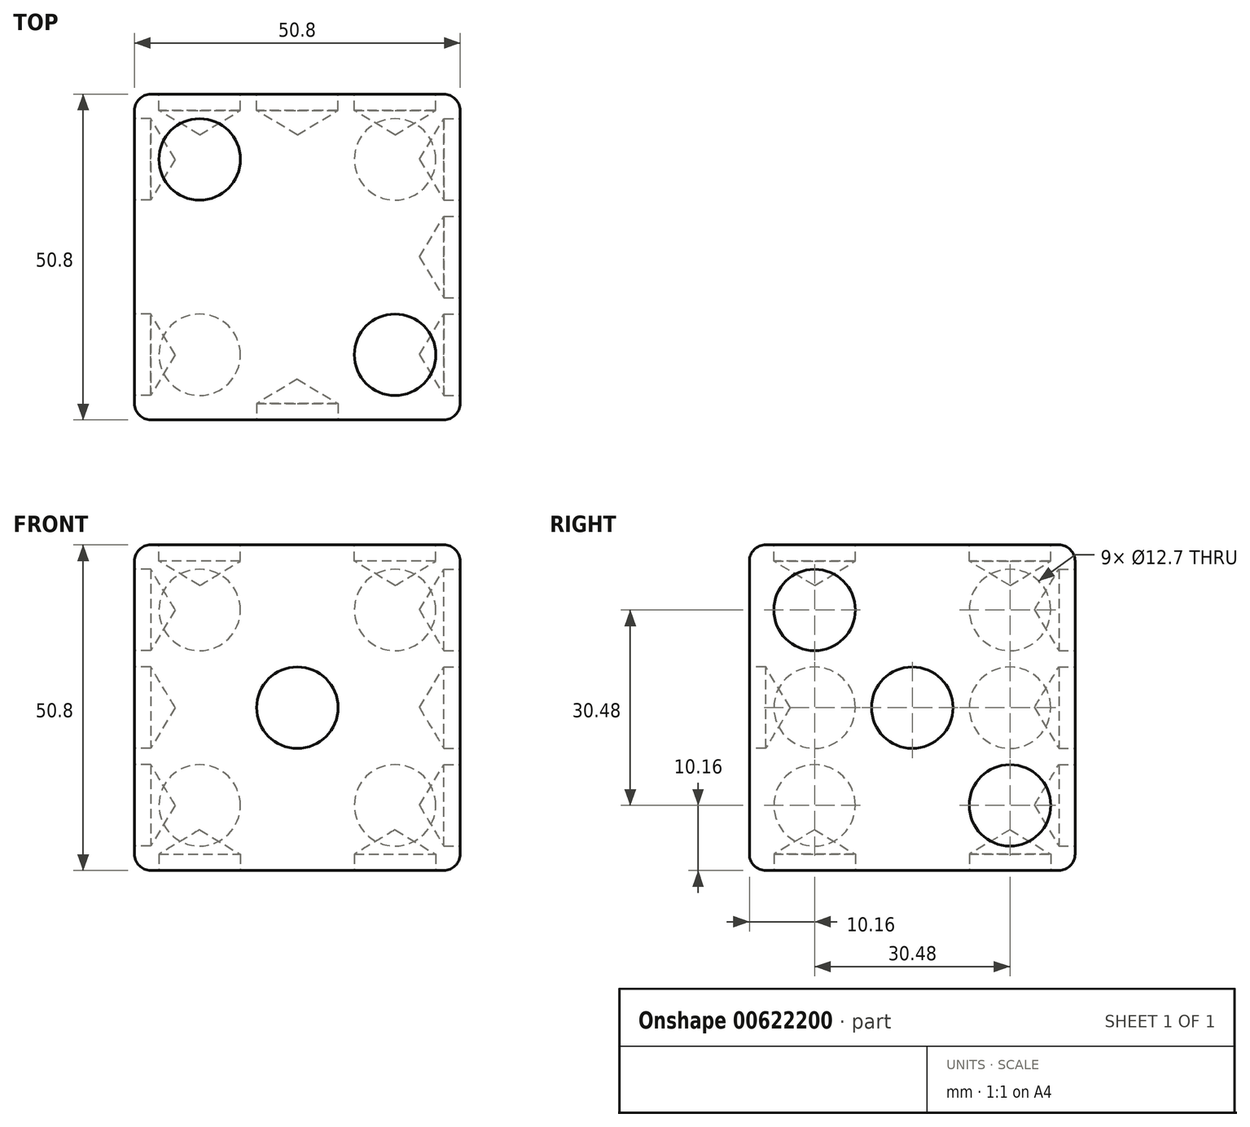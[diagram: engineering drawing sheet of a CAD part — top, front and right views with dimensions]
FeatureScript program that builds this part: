
annotation { "Feature Type Name" : "Feature", "Feature Type Description" : "" }
export const myFeature = defineFeature(function(context is Context, id is Id, definition is map)
    precondition{}
    {
        {
            var Q0;
            Q0=qCreatedBy(makeId("Front.planeOp"),FACE);
            var sketch = newSketch(context, id + "F0", { "sketchPlane" : qUnion([Q0])});
            skLineSegment(sketch, "E0.bottom", {"start": v(25.4, -25.4) * mm, "end": v(-25.4, -25.4) * mm});
            skLineSegment(sketch, "E0.top", {"start": v(25.4, 25.4) * mm, "end": v(-25.4, 25.4) * mm});
            skLineSegment(sketch, "E0.left", {"start": v(25.4, -25.4) * mm, "end": v(25.4, 25.4) * mm});
            skLineSegment(sketch, "E0.right", {"start": v(-25.4, -25.4) * mm, "end": v(-25.4, 25.4) * mm});
            skPoint(sketch, "E0.middle", {"position": v(0, 0) * mm});
            skSolve(sketch);
        }
        {
            var Q0;
            Q0 = qSketchRegion(id + "F0", true);
            extrude(context, id + "F1", {"entities" : qUnion([Q0]), "endBound" : BoundingType.SYMMETRIC, "depth" : 50.8 * mm, "offsetDistance" : 25.4 * mm});
        }
        {
            var Q0;
            Q0=makeQuery(id+"F1.opExtrude","CAP_FACE",FACE,{"disambiguationData":[OSD([sQuery(id+"F0.wireOp",EDGE,"E0.bottom"),sQuery(id+"F0.wireOp",EDGE,"E0.top"),sQuery(id+"F0.wireOp",EDGE,"E0.left"),sQuery(id+"F0.wireOp",EDGE,"E0.right")])],"isStart":false});
            var sketch = newSketch(context, id + "F2", { "sketchPlane" : qUnion([Q0])});
            skCircle(sketch, "E1", {"center": v(0, 0) * mm, "radius": 6.35 * mm});
            skSolve(sketch);
        }
        {
            var Q0;
            Q0=sQuery(id+"F2.wireOp",VERTEX,"E1.center");
            var Q1;
            Q1=makeQuery(id+"F1.opExtrude","SWEPT_BODY",BODY,{"disambiguationData":[OSD([sQuery(id+"F0.wireOp",EDGE,"E0.bottom"),sQuery(id+"F0.wireOp",EDGE,"E0.top"),sQuery(id+"F0.wireOp",EDGE,"E0.left"),sQuery(id+"F0.wireOp",EDGE,"E0.right")])]});
            hole(context, id + "F3", {"style" : HoleStyle.SIMPLE, "endStyle" : HoleEndStyle.BLIND, "holeDiameter" : 12.7 * mm, "majorDiameter" : 6.35 * mm, "holeDepth" : 2.54 * mm, "isTappedThrough" : true, "tappedDepth" : 12.7 * mm, "tapClearance" : 3, "startFromSketch" : true, "locations" : qUnion([Q0]), "scope" : qUnion([Q1])});
        }
        {
            var Q0;
            Q0=makeQuery(id+"F1.opExtrude","CAP_FACE",FACE,{"disambiguationData":[OSD([sQuery(id+"F0.wireOp",EDGE,"E0.bottom"),sQuery(id+"F0.wireOp",EDGE,"E0.top"),sQuery(id+"F0.wireOp",EDGE,"E0.left"),sQuery(id+"F0.wireOp",EDGE,"E0.right")])],"isStart":true});
            var sketch = newSketch(context, id + "F4", { "sketchPlane" : qUnion([Q0])});
            skCircle(sketch, "E2", {"center": v(0, 0) * mm, "radius": 6.35 * mm});
            skCircle(sketch, "E3", {"center": v(-15.24, 15.24) * mm, "radius": 6.35 * mm});
            skCircle(sketch, "E4", {"center": v(15.24, -15.24) * mm, "radius": 6.35 * mm});
            skSolve(sketch);
        }
        {
            var Q0;
            Q0=sQuery(id+"F4.wireOp",VERTEX,"E3.center");
            var Q1;
            Q1=sQuery(id+"F4.wireOp",VERTEX,"E2.center");
            var Q2;
            Q2=sQuery(id+"F4.wireOp",VERTEX,"E4.center");
            var Q3;
            Q3=makeQuery(id+"F1.opExtrude","SWEPT_BODY",BODY,{"disambiguationData":[OSD([sQuery(id+"F0.wireOp",EDGE,"E0.bottom"),sQuery(id+"F0.wireOp",EDGE,"E0.top"),sQuery(id+"F0.wireOp",EDGE,"E0.left"),sQuery(id+"F0.wireOp",EDGE,"E0.right")])]});
            hole(context, id + "F5", {"style" : HoleStyle.SIMPLE, "endStyle" : HoleEndStyle.BLIND, "holeDiameter" : 12.7 * mm, "majorDiameter" : 6.35 * mm, "holeDepth" : 2.54 * mm, "isTappedThrough" : true, "tappedDepth" : 12.7 * mm, "tapClearance" : 3, "startFromSketch" : true, "locations" : qUnion([Q0, Q1, Q2]), "scope" : qUnion([Q3])});
        }
        {
            var Q0;
            Q0=makeQuery(id+"F1.opExtrude","SWEPT_FACE",FACE,{"disambiguationData":[OSD([sQuery(id+"F0.wireOp",EDGE,"E0.top")])]});
            var sketch = newSketch(context, id + "F6", { "sketchPlane" : qUnion([Q0])});
            skCircle(sketch, "E5", {"center": v(-15.24, 15.24) * mm, "radius": 6.35 * mm});
            skCircle(sketch, "E6", {"center": v(15.24, -15.24) * mm, "radius": 6.35 * mm});
            skSolve(sketch);
        }
        {
            var Q0;
            Q0=sQuery(id+"F6.wireOp",VERTEX,"E5.center");
            var Q1;
            Q1=sQuery(id+"F6.wireOp",VERTEX,"E6.center");
            var Q2;
            Q2=makeQuery(id+"F1.opExtrude","SWEPT_BODY",BODY,{"disambiguationData":[OSD([sQuery(id+"F0.wireOp",EDGE,"E0.bottom"),sQuery(id+"F0.wireOp",EDGE,"E0.top"),sQuery(id+"F0.wireOp",EDGE,"E0.left"),sQuery(id+"F0.wireOp",EDGE,"E0.right")])]});
            hole(context, id + "F7", {"style" : HoleStyle.SIMPLE, "endStyle" : HoleEndStyle.BLIND, "holeDiameter" : 12.7 * mm, "majorDiameter" : 6.35 * mm, "holeDepth" : 2.54 * mm, "isTappedThrough" : true, "tappedDepth" : 12.7 * mm, "tapClearance" : 3, "startFromSketch" : true, "locations" : qUnion([Q0, Q1]), "scope" : qUnion([Q2])});
        }
        {
            var Q0;
            Q0=makeQuery(id+"F1.opExtrude","SWEPT_FACE",FACE,{"disambiguationData":[OSD([sQuery(id+"F0.wireOp",EDGE,"E0.bottom")])]});
            var sketch = newSketch(context, id + "F8", { "sketchPlane" : qUnion([Q0])});
            skCircle(sketch, "E7", {"center": v(-15.24, 15.24) * mm, "radius": 6.35 * mm});
            skCircle(sketch, "E8", {"center": v(15.24, 15.24) * mm, "radius": 6.35 * mm});
            skCircle(sketch, "E9", {"center": v(-15.24, -15.24) * mm, "radius": 6.35 * mm});
            skCircle(sketch, "E10", {"center": v(15.24, -15.24) * mm, "radius": 6.35 * mm});
            skSolve(sketch);
        }
        {
            var Q0;
            Q0=sQuery(id+"F8.wireOp",VERTEX,"E7.center");
            var Q1;
            Q1=sQuery(id+"F8.wireOp",VERTEX,"E8.center");
            var Q2;
            Q2=sQuery(id+"F8.wireOp",VERTEX,"E10.center");
            var Q3;
            Q3=sQuery(id+"F8.wireOp",VERTEX,"E9.center");
            var Q4;
            Q4=makeQuery(id+"F1.opExtrude","SWEPT_BODY",BODY,{"disambiguationData":[OSD([sQuery(id+"F0.wireOp",EDGE,"E0.bottom"),sQuery(id+"F0.wireOp",EDGE,"E0.top"),sQuery(id+"F0.wireOp",EDGE,"E0.left"),sQuery(id+"F0.wireOp",EDGE,"E0.right")])]});
            hole(context, id + "F9", {"style" : HoleStyle.SIMPLE, "endStyle" : HoleEndStyle.BLIND, "holeDiameter" : 12.7 * mm, "majorDiameter" : 6.35 * mm, "holeDepth" : 2.54 * mm, "isTappedThrough" : true, "tappedDepth" : 12.7 * mm, "tapClearance" : 3, "startFromSketch" : true, "locations" : qUnion([Q0, Q1, Q2, Q3]), "scope" : qUnion([Q4])});
        }
        {
            var Q0;
            Q0=makeQuery(id+"F1.opExtrude","CAP_FACE",FACE,{"disambiguationData":[OSD([sQuery(id+"F0.wireOp",EDGE,"E0.bottom"),sQuery(id+"F0.wireOp",EDGE,"E0.top"),sQuery(id+"F0.wireOp",EDGE,"E0.left"),sQuery(id+"F0.wireOp",EDGE,"E0.right")])],"isStart":true});
            var sketch = newSketch(context, id + "F10", { "sketchPlane" : qUnion([Q0])});
            skSolve(sketch);
        }
        {
            var Q0;
            Q0=makeQuery(id+"F10.imprint","IMPRINT",FACE,{"disambiguationData":[TD([[makeQuery(id+"F10.imprint","IMPRINT",EDGE,{"derivedFrom":makeQuery(id+"F1.opExtrude","CAP_EDGE",EDGE,{"disambiguationData":[OSD([sQuery(id+"F0.wireOp",EDGE,"E0.bottom")])],"isStart":true})}),1.0]])]});
            var sketch = newSketch(context, id + "F11", { "sketchPlane" : qUnion([Q0])});
            skCircle(sketch, "E11", {"center": v(15.24, 15.24) * mm, "radius": 6.35 * mm});
            skCircle(sketch, "E12", {"center": v(-15.24, -15.24) * mm, "radius": 6.35 * mm});
            skSolve(sketch);
        }
        {
            var Q0;
            Q0=sQuery(id+"F11.wireOp",VERTEX,"E11.center");
            var Q1;
            Q1=sQuery(id+"F11.wireOp",VERTEX,"E12.center");
            var Q2;
            Q2=makeQuery(id+"F1.opExtrude","SWEPT_BODY",BODY,{"disambiguationData":[OSD([sQuery(id+"F0.wireOp",EDGE,"E0.bottom"),sQuery(id+"F0.wireOp",EDGE,"E0.top"),sQuery(id+"F0.wireOp",EDGE,"E0.left"),sQuery(id+"F0.wireOp",EDGE,"E0.right")])]});
            hole(context, id + "F12", {"style" : HoleStyle.SIMPLE, "endStyle" : HoleEndStyle.BLIND, "holeDiameter" : 12.7 * mm, "majorDiameter" : 6.35 * mm, "holeDepth" : 2.54 * mm, "isTappedThrough" : true, "tappedDepth" : 12.7 * mm, "tapClearance" : 3, "startFromSketch" : true, "locations" : qUnion([Q0, Q1]), "scope" : qUnion([Q2])});
        }
        {
            var Q0;
            Q0=makeQuery(id+"F1.opExtrude","SWEPT_FACE",FACE,{"disambiguationData":[OSD([sQuery(id+"F0.wireOp",EDGE,"E0.left")])]});
            var sketch = newSketch(context, id + "F13", { "sketchPlane" : qUnion([Q0])});
            skCircle(sketch, "E13", {"center": v(-15.24, 15.24) * mm, "radius": 6.35 * mm});
            skCircle(sketch, "E14", {"center": v(0, 0) * mm, "radius": 6.35 * mm});
            skCircle(sketch, "E15", {"center": v(15.24, -15.24) * mm, "radius": 6.35 * mm});
            skSolve(sketch);
        }
        {
            var Q0;
            Q0=sQuery(id+"F13.wireOp",VERTEX,"E13.center");
            var Q1;
            Q1=sQuery(id+"F13.wireOp",VERTEX,"E14.center");
            var Q2;
            Q2=sQuery(id+"F13.wireOp",VERTEX,"E15.center");
            var Q3;
            Q3=makeQuery(id+"F1.opExtrude","SWEPT_BODY",BODY,{"disambiguationData":[OSD([sQuery(id+"F0.wireOp",EDGE,"E0.bottom"),sQuery(id+"F0.wireOp",EDGE,"E0.top"),sQuery(id+"F0.wireOp",EDGE,"E0.left"),sQuery(id+"F0.wireOp",EDGE,"E0.right")])]});
            hole(context, id + "F14", {"style" : HoleStyle.SIMPLE, "endStyle" : HoleEndStyle.BLIND, "holeDiameter" : 12.7 * mm, "majorDiameter" : 6.35 * mm, "holeDepth" : 2.54 * mm, "isTappedThrough" : true, "tappedDepth" : 12.7 * mm, "tapClearance" : 3, "startFromSketch" : true, "locations" : qUnion([Q0, Q1, Q2]), "scope" : qUnion([Q3])});
        }
        {
            var Q0;
            Q0=makeQuery(id+"F1.opExtrude","SWEPT_FACE",FACE,{"disambiguationData":[OSD([sQuery(id+"F0.wireOp",EDGE,"E0.right")])]});
            var sketch = newSketch(context, id + "F15", { "sketchPlane" : qUnion([Q0])});
            skCircle(sketch, "E16", {"center": v(-15.24, 15.24) * mm, "radius": 6.35 * mm});
            skCircle(sketch, "E17", {"center": v(-15.24, 0) * mm, "radius": 6.35 * mm});
            skCircle(sketch, "E18", {"center": v(-15.24, -15.24) * mm, "radius": 6.35 * mm});
            skCircle(sketch, "E19", {"center": v(15.24, 15.24) * mm, "radius": 6.35 * mm});
            skCircle(sketch, "E20", {"center": v(15.24, 0) * mm, "radius": 6.35 * mm});
            skCircle(sketch, "E21", {"center": v(15.24, -15.24) * mm, "radius": 6.35 * mm});
            skSolve(sketch);
        }
        {
            var Q0;
            Q0=sQuery(id+"F15.wireOp",VERTEX,"E16.center");
            var Q1;
            Q1=sQuery(id+"F15.wireOp",VERTEX,"E17.center");
            var Q2;
            Q2=sQuery(id+"F15.wireOp",VERTEX,"E18.center");
            var Q3;
            Q3=sQuery(id+"F15.wireOp",VERTEX,"E21.center");
            var Q4;
            Q4=sQuery(id+"F15.wireOp",VERTEX,"E20.center");
            var Q5;
            Q5=sQuery(id+"F15.wireOp",VERTEX,"E19.center");
            var Q6;
            Q6=makeQuery(id+"F1.opExtrude","SWEPT_BODY",BODY,{"disambiguationData":[OSD([sQuery(id+"F0.wireOp",EDGE,"E0.bottom"),sQuery(id+"F0.wireOp",EDGE,"E0.top"),sQuery(id+"F0.wireOp",EDGE,"E0.left"),sQuery(id+"F0.wireOp",EDGE,"E0.right")])]});
            hole(context, id + "F16", {"style" : HoleStyle.SIMPLE, "endStyle" : HoleEndStyle.BLIND, "holeDiameter" : 12.7 * mm, "majorDiameter" : 6.35 * mm, "holeDepth" : 2.54 * mm, "isTappedThrough" : true, "tappedDepth" : 12.7 * mm, "tapClearance" : 3, "startFromSketch" : true, "locations" : qUnion([Q0, Q1, Q2, Q3, Q4, Q5]), "scope" : qUnion([Q6])});
        }
        {
            var Q0;
            Q0=makeQuery(id+"F1.opExtrude","SWEPT_EDGE",EDGE,{"disambiguationData":[OSD([sQuery(id+"F0.wireOp",EDGE,"E0.top"),sQuery(id+"F0.wireOp",EDGE,"E0.right")])]});
            var Q1;
            Q1=makeQuery(id+"F1.opExtrude","CAP_EDGE",EDGE,{"disambiguationData":[OSD([sQuery(id+"F0.wireOp",EDGE,"E0.top")])],"isStart":true});
            var Q2;
            Q2=makeQuery(id+"F1.opExtrude","CAP_EDGE",EDGE,{"disambiguationData":[OSD([sQuery(id+"F0.wireOp",EDGE,"E0.right")])],"isStart":true});
            var Q3;
            Q3=makeQuery(id+"F1.opExtrude","CAP_EDGE",EDGE,{"disambiguationData":[OSD([sQuery(id+"F0.wireOp",EDGE,"E0.top")])],"isStart":false});
            var Q4;
            Q4=makeQuery(id+"F1.opExtrude","SWEPT_EDGE",EDGE,{"disambiguationData":[OSD([sQuery(id+"F0.wireOp",EDGE,"E0.top"),sQuery(id+"F0.wireOp",EDGE,"E0.left")])]});
            var Q5;
            Q5=makeQuery(id+"F1.opExtrude","CAP_EDGE",EDGE,{"disambiguationData":[OSD([sQuery(id+"F0.wireOp",EDGE,"E0.left")])],"isStart":true});
            var Q6;
            Q6=makeQuery(id+"F1.opExtrude","CAP_EDGE",EDGE,{"disambiguationData":[OSD([sQuery(id+"F0.wireOp",EDGE,"E0.left")])],"isStart":false});
            var Q7;
            Q7=makeQuery(id+"F1.opExtrude","SWEPT_EDGE",EDGE,{"disambiguationData":[OSD([sQuery(id+"F0.wireOp",EDGE,"E0.bottom"),sQuery(id+"F0.wireOp",EDGE,"E0.left")])]});
            var Q8;
            Q8=makeQuery(id+"F1.opExtrude","CAP_EDGE",EDGE,{"disambiguationData":[OSD([sQuery(id+"F0.wireOp",EDGE,"E0.bottom")])],"isStart":true});
            var Q9;
            Q9=makeQuery(id+"F1.opExtrude","SWEPT_EDGE",EDGE,{"disambiguationData":[OSD([sQuery(id+"F0.wireOp",EDGE,"E0.bottom"),sQuery(id+"F0.wireOp",EDGE,"E0.right")])]});
            var Q10;
            Q10=makeQuery(id+"F1.opExtrude","CAP_EDGE",EDGE,{"disambiguationData":[OSD([sQuery(id+"F0.wireOp",EDGE,"E0.right")])],"isStart":false});
            var Q11;
            Q11=makeQuery(id+"F1.opExtrude","CAP_EDGE",EDGE,{"disambiguationData":[OSD([sQuery(id+"F0.wireOp",EDGE,"E0.bottom")])],"isStart":false});
            fillet(context, id + "F17", {"entities" : qUnion([Q0, Q1, Q2, Q3, Q4, Q5, Q6, Q7, Q8, Q9, Q10, Q11]), "radius" : 2.54 * mm, "tangentPropagation" : true, "allowEdgeOverflow" : false});
        }
    });
